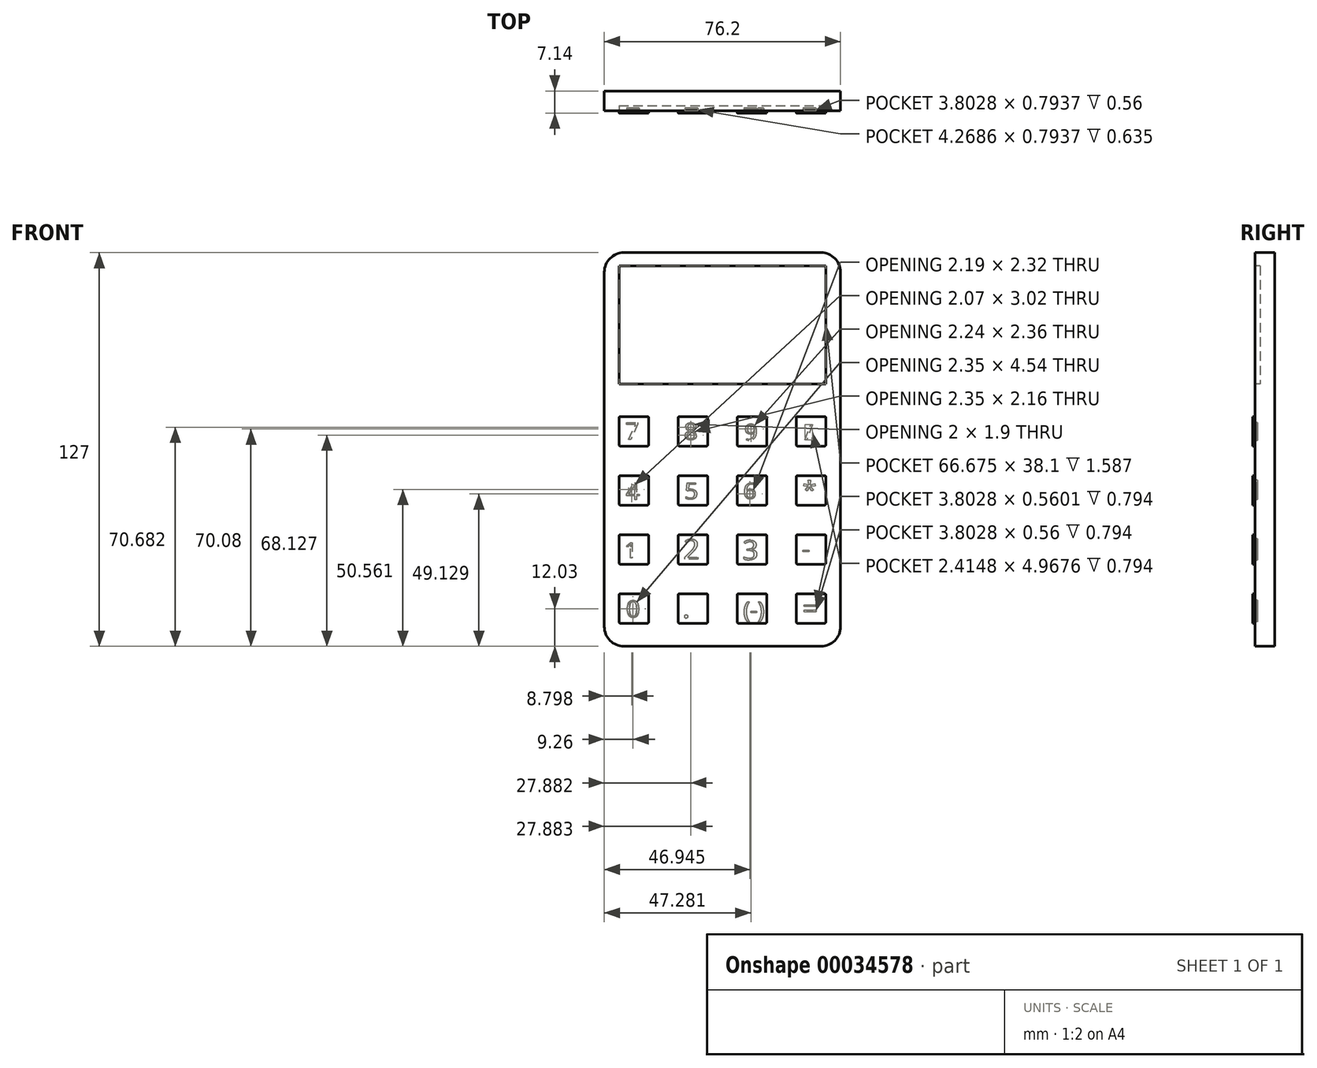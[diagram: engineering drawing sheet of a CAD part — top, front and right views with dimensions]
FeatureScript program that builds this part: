
annotation { "Feature Type Name" : "Feature", "Feature Type Description" : "" }
export const myFeature = defineFeature(function(context is Context, id is Id, definition is map)
    precondition{}
    {
        {
            var Q0;
            Q0=qCreatedBy(makeId("Front.planeOp"),FACE);
            var sketch = newSketch(context, id + "F0", { "sketchPlane" : qUnion([Q0])});
            skLineSegment(sketch, "E0.bottom", {"start": v(-54.14, 62.32) * mm, "end": v(22.06, 62.32) * mm});
            skLineSegment(sketch, "E0.top", {"start": v(-54.14, -64.68) * mm, "end": v(22.06, -64.68) * mm});
            skLineSegment(sketch, "E0.left", {"start": v(-54.14, 62.32) * mm, "end": v(-54.14, -64.68) * mm});
            skLineSegment(sketch, "E0.right", {"start": v(22.06, 62.32) * mm, "end": v(22.06, -64.68) * mm});
            skSolve(sketch);
        }
        {
            var Q0;
            Q0=makeQuery(id+"F0.imprint","IMPRINT",FACE,{"disambiguationData":[TD([[makeQuery(id+"F0.imprint","IMPRINT",EDGE,{"derivedFrom":sQuery(id+"F0.wireOp",EDGE,"E0.bottom")}),-1.0]])]});
            extrude(context, id + "F1", {"entities" : qUnion([Q0]), "depth" : 6.35 * mm});
        }
        {
            var Q0;
            Q0=makeQuery(id+"F1.opExtrude","CAP_FACE",FACE,{"disambiguationData":[OSD([sQuery(id+"F0.wireOp",EDGE,"E0.bottom"),sQuery(id+"F0.wireOp",EDGE,"E0.top"),sQuery(id+"F0.wireOp",EDGE,"E0.left"),sQuery(id+"F0.wireOp",EDGE,"E0.right")])],"isStart":false});
            var sketch = newSketch(context, id + "F2", { "sketchPlane" : qUnion([Q0])});
            skLineSegment(sketch, "E1.bottom", {"start": v(-49.38, 58.02) * mm, "end": v(17.3, 58.02) * mm});
            skLineSegment(sketch, "E1.top", {"start": v(-49.38, 19.92) * mm, "end": v(17.3, 19.92) * mm});
            skLineSegment(sketch, "E1.left", {"start": v(-49.38, 58.02) * mm, "end": v(-49.38, 19.92) * mm});
            skLineSegment(sketch, "E1.right", {"start": v(17.3, 58.02) * mm, "end": v(17.3, 19.92) * mm});
            skSolve(sketch);
        }
        {
            var Q0;
            Q0=makeQuery(id+"F2.imprint","IMPRINT",FACE,{"disambiguationData":[TD([[makeQuery(id+"F2.imprint","IMPRINT",EDGE,{"derivedFrom":sQuery(id+"F2.wireOp",EDGE,"E1.bottom")}),-1.0]])]});
            extrude(context, id + "F3", {"entities" : qUnion([Q0]), "operationType" : NewBodyOperationType.REMOVE, "oppositeDirection" : true, "depth" : 1.59 * mm});
        }
        {
            var Q0;
            Q0=makeQuery(id+"F1.opExtrude","SWEPT_EDGE",EDGE,{"disambiguationData":[OSD([sQuery(id+"F0.wireOp",EDGE,"E0.bottom"),sQuery(id+"F0.wireOp",EDGE,"E0.left")])]});
            var Q1;
            Q1=makeQuery(id+"F1.opExtrude","SWEPT_EDGE",EDGE,{"disambiguationData":[OSD([sQuery(id+"F0.wireOp",EDGE,"E0.bottom"),sQuery(id+"F0.wireOp",EDGE,"E0.right")])]});
            var Q2;
            Q2=makeQuery(id+"F1.opExtrude","SWEPT_EDGE",EDGE,{"disambiguationData":[OSD([sQuery(id+"F0.wireOp",EDGE,"E0.top"),sQuery(id+"F0.wireOp",EDGE,"E0.right")])]});
            var Q3;
            Q3=makeQuery(id+"F1.opExtrude","SWEPT_EDGE",EDGE,{"disambiguationData":[OSD([sQuery(id+"F0.wireOp",EDGE,"E0.top"),sQuery(id+"F0.wireOp",EDGE,"E0.left")])]});
            fillet(context, id + "F4", {"entities" : qUnion([Q0, Q1, Q2, Q3]), "radius" : 6.35 * mm, "tangentPropagation" : true, "allowEdgeOverflow" : false});
        }
        {
            var Q0;
            Q0=makeQuery(id+"F1.opExtrude","CAP_FACE",FACE,{"disambiguationData":[OSD([sQuery(id+"F0.wireOp",EDGE,"E0.bottom"),sQuery(id+"F0.wireOp",EDGE,"E0.top"),sQuery(id+"F0.wireOp",EDGE,"E0.left"),sQuery(id+"F0.wireOp",EDGE,"E0.right")])],"isStart":false});
            var sketch = newSketch(context, id + "F5", { "sketchPlane" : qUnion([Q0])});
            skLineSegment(sketch, "E2.bottom", {"start": v(-49.38, -47.74) * mm, "end": v(-39.86, -47.74) * mm});
            skLineSegment(sketch, "E2.top", {"start": v(-49.38, -57.27) * mm, "end": v(-39.86, -57.27) * mm});
            skLineSegment(sketch, "E2.left", {"start": v(-49.38, -47.74) * mm, "end": v(-49.38, -57.27) * mm});
            skLineSegment(sketch, "E2.right", {"start": v(-39.86, -47.74) * mm, "end": v(-39.86, -57.27) * mm});
            skLineSegment(sketch, "E3.0.1.0", {"start": v(-49.38, -28.7) * mm, "end": v(-49.38, -38.22) * mm});
            skLineSegment(sketch, "E3.0.1.1", {"start": v(-49.38, -38.22) * mm, "end": v(-39.86, -38.22) * mm});
            skLineSegment(sketch, "E3.0.1.2", {"start": v(-49.38, -28.7) * mm, "end": v(-39.86, -28.7) * mm});
            skLineSegment(sketch, "E3.0.1.3", {"start": v(-39.86, -28.7) * mm, "end": v(-39.86, -38.22) * mm});
            skLineSegment(sketch, "E3.0.2.0", {"start": v(-49.38, -9.64) * mm, "end": v(-49.38, -19.17) * mm});
            skLineSegment(sketch, "E3.0.2.1", {"start": v(-49.38, -19.17) * mm, "end": v(-39.86, -19.17) * mm});
            skLineSegment(sketch, "E3.0.2.2", {"start": v(-49.38, -9.64) * mm, "end": v(-39.86, -9.64) * mm});
            skLineSegment(sketch, "E3.0.2.3", {"start": v(-39.86, -9.64) * mm, "end": v(-39.86, -19.17) * mm});
            skLineSegment(sketch, "E3.0.3.0", {"start": v(-49.38, 9.4) * mm, "end": v(-49.38, -0.12) * mm});
            skLineSegment(sketch, "E3.0.3.1", {"start": v(-49.38, -0.12) * mm, "end": v(-39.86, -0.12) * mm});
            skLineSegment(sketch, "E3.0.3.2", {"start": v(-49.38, 9.4) * mm, "end": v(-39.86, 9.4) * mm});
            skLineSegment(sketch, "E3.0.3.3", {"start": v(-39.86, 9.4) * mm, "end": v(-39.86, -0.12) * mm});
            skLineSegment(sketch, "E3.1.0.0", {"start": v(-30.33, -47.74) * mm, "end": v(-30.33, -57.27) * mm});
            skLineSegment(sketch, "E3.1.0.1", {"start": v(-30.33, -57.27) * mm, "end": v(-20.8, -57.27) * mm});
            skLineSegment(sketch, "E3.1.0.2", {"start": v(-30.33, -47.74) * mm, "end": v(-20.8, -47.74) * mm});
            skLineSegment(sketch, "E3.1.0.3", {"start": v(-20.8, -47.74) * mm, "end": v(-20.8, -57.27) * mm});
            skLineSegment(sketch, "E3.1.1.0", {"start": v(-30.33, -28.7) * mm, "end": v(-30.33, -38.22) * mm});
            skLineSegment(sketch, "E3.1.1.1", {"start": v(-30.33, -38.22) * mm, "end": v(-20.8, -38.22) * mm});
            skLineSegment(sketch, "E3.1.1.2", {"start": v(-30.33, -28.7) * mm, "end": v(-20.8, -28.7) * mm});
            skLineSegment(sketch, "E3.1.1.3", {"start": v(-20.8, -28.7) * mm, "end": v(-20.8, -38.22) * mm});
            skLineSegment(sketch, "E3.1.2.0", {"start": v(-30.33, -9.64) * mm, "end": v(-30.33, -19.17) * mm});
            skLineSegment(sketch, "E3.1.2.1", {"start": v(-30.33, -19.17) * mm, "end": v(-20.8, -19.17) * mm});
            skLineSegment(sketch, "E3.1.2.2", {"start": v(-30.33, -9.64) * mm, "end": v(-20.8, -9.64) * mm});
            skLineSegment(sketch, "E3.1.2.3", {"start": v(-20.8, -9.64) * mm, "end": v(-20.8, -19.17) * mm});
            skLineSegment(sketch, "E3.1.3.0", {"start": v(-30.33, 9.4) * mm, "end": v(-30.33, -0.12) * mm});
            skLineSegment(sketch, "E3.1.3.1", {"start": v(-30.33, -0.12) * mm, "end": v(-20.8, -0.12) * mm});
            skLineSegment(sketch, "E3.1.3.2", {"start": v(-30.33, 9.4) * mm, "end": v(-20.8, 9.4) * mm});
            skLineSegment(sketch, "E3.1.3.3", {"start": v(-20.8, 9.4) * mm, "end": v(-20.8, -0.12) * mm});
            skLineSegment(sketch, "E3.2.0.0", {"start": v(-11.28, -47.74) * mm, "end": v(-11.28, -57.27) * mm});
            skLineSegment(sketch, "E3.2.0.1", {"start": v(-11.28, -57.27) * mm, "end": v(-1.76, -57.27) * mm});
            skLineSegment(sketch, "E3.2.0.2", {"start": v(-11.28, -47.74) * mm, "end": v(-1.76, -47.74) * mm});
            skLineSegment(sketch, "E3.2.0.3", {"start": v(-1.76, -47.74) * mm, "end": v(-1.76, -57.27) * mm});
            skLineSegment(sketch, "E3.2.1.0", {"start": v(-11.28, -28.7) * mm, "end": v(-11.28, -38.22) * mm});
            skLineSegment(sketch, "E3.2.1.1", {"start": v(-11.28, -38.22) * mm, "end": v(-1.76, -38.22) * mm});
            skLineSegment(sketch, "E3.2.1.2", {"start": v(-11.28, -28.7) * mm, "end": v(-1.76, -28.7) * mm});
            skLineSegment(sketch, "E3.2.1.3", {"start": v(-1.76, -28.7) * mm, "end": v(-1.76, -38.22) * mm});
            skLineSegment(sketch, "E3.2.2.0", {"start": v(-11.28, -9.64) * mm, "end": v(-11.28, -19.17) * mm});
            skLineSegment(sketch, "E3.2.2.1", {"start": v(-11.28, -19.17) * mm, "end": v(-1.76, -19.17) * mm});
            skLineSegment(sketch, "E3.2.2.2", {"start": v(-11.28, -9.64) * mm, "end": v(-1.76, -9.64) * mm});
            skLineSegment(sketch, "E3.2.2.3", {"start": v(-1.76, -9.64) * mm, "end": v(-1.76, -19.17) * mm});
            skLineSegment(sketch, "E3.2.3.0", {"start": v(-11.28, 9.4) * mm, "end": v(-11.28, -0.12) * mm});
            skLineSegment(sketch, "E3.2.3.1", {"start": v(-11.28, -0.12) * mm, "end": v(-1.76, -0.12) * mm});
            skLineSegment(sketch, "E3.2.3.2", {"start": v(-11.28, 9.4) * mm, "end": v(-1.76, 9.4) * mm});
            skLineSegment(sketch, "E3.2.3.3", {"start": v(-1.76, 9.4) * mm, "end": v(-1.76, -0.12) * mm});
            skLineSegment(sketch, "E3.3.0.0", {"start": v(7.77, -47.74) * mm, "end": v(7.77, -57.27) * mm});
            skLineSegment(sketch, "E3.3.0.1", {"start": v(7.77, -57.27) * mm, "end": v(17.3, -57.27) * mm});
            skLineSegment(sketch, "E3.3.0.2", {"start": v(7.77, -47.74) * mm, "end": v(17.3, -47.74) * mm});
            skLineSegment(sketch, "E3.3.0.3", {"start": v(17.3, -47.74) * mm, "end": v(17.3, -57.27) * mm});
            skLineSegment(sketch, "E3.3.1.0", {"start": v(7.77, -28.7) * mm, "end": v(7.77, -38.22) * mm});
            skLineSegment(sketch, "E3.3.1.1", {"start": v(7.77, -38.22) * mm, "end": v(17.3, -38.22) * mm});
            skLineSegment(sketch, "E3.3.1.2", {"start": v(7.77, -28.7) * mm, "end": v(17.3, -28.7) * mm});
            skLineSegment(sketch, "E3.3.1.3", {"start": v(17.3, -28.7) * mm, "end": v(17.3, -38.22) * mm});
            skLineSegment(sketch, "E3.3.2.0", {"start": v(7.77, -9.64) * mm, "end": v(7.77, -19.17) * mm});
            skLineSegment(sketch, "E3.3.2.1", {"start": v(7.77, -19.17) * mm, "end": v(17.3, -19.17) * mm});
            skLineSegment(sketch, "E3.3.2.2", {"start": v(7.77, -9.64) * mm, "end": v(17.3, -9.64) * mm});
            skLineSegment(sketch, "E3.3.2.3", {"start": v(17.3, -9.64) * mm, "end": v(17.3, -19.17) * mm});
            skLineSegment(sketch, "E3.3.3.0", {"start": v(7.77, 9.4) * mm, "end": v(7.77, -0.12) * mm});
            skLineSegment(sketch, "E3.3.3.1", {"start": v(7.77, -0.12) * mm, "end": v(17.3, -0.12) * mm});
            skLineSegment(sketch, "E3.3.3.2", {"start": v(7.77, 9.4) * mm, "end": v(17.3, 9.4) * mm});
            skLineSegment(sketch, "E3.3.3.3", {"start": v(17.3, 9.4) * mm, "end": v(17.3, -0.12) * mm});
            skLineSegment(sketch, "E3.direction1", {"start": v(-49.38, -57.27) * mm, "end": v(-30.33, -57.27) * mm, "construction": true});
            skLineSegment(sketch, "E3.direction2", {"start": v(-49.38, -57.27) * mm, "end": v(-49.38, -38.22) * mm, "construction": true});
            skSolve(sketch);
        }
        {
            var Q0;
            Q0 = qSketchRegion(id + "F5", true);
            extrude(context, id + "F6", {"entities" : qUnion([Q0]), "operationType" : NewBodyOperationType.ADD, "depth" : 0.8 * mm});
        }
        {
            var Q0;
            Q0=makeQuery(id+"F6.opExtrude","SWEPT_EDGE",EDGE,{"disambiguationData":[OSD([sQuery(id+"F5.wireOp",EDGE,"E3.0.3.0"),sQuery(id+"F5.wireOp",EDGE,"E3.0.3.2")])]});
            var Q1;
            Q1=makeQuery(id+"F6.opExtrude","SWEPT_EDGE",EDGE,{"disambiguationData":[OSD([sQuery(id+"F5.wireOp",EDGE,"E3.0.2.0"),sQuery(id+"F5.wireOp",EDGE,"E3.0.2.2")])]});
            var Q2;
            Q2=makeQuery(id+"F6.opExtrude","SWEPT_EDGE",EDGE,{"disambiguationData":[OSD([sQuery(id+"F5.wireOp",EDGE,"E3.0.1.0"),sQuery(id+"F5.wireOp",EDGE,"E3.0.1.2")])]});
            var Q3;
            Q3=makeQuery(id+"F6.opExtrude","SWEPT_EDGE",EDGE,{"disambiguationData":[OSD([sQuery(id+"F5.wireOp",EDGE,"E2.bottom"),sQuery(id+"F5.wireOp",EDGE,"E2.left")])]});
            var Q4;
            Q4=makeQuery(id+"F6.opExtrude","SWEPT_EDGE",EDGE,{"disambiguationData":[OSD([sQuery(id+"F5.wireOp",EDGE,"E2.top"),sQuery(id+"F5.wireOp",EDGE,"E2.left")])]});
            var Q5;
            Q5=makeQuery(id+"F6.opExtrude","SWEPT_EDGE",EDGE,{"disambiguationData":[OSD([sQuery(id+"F5.wireOp",EDGE,"E3.1.0.0"),sQuery(id+"F5.wireOp",EDGE,"E3.1.0.1")])]});
            var Q6;
            Q6=makeQuery(id+"F6.opExtrude","SWEPT_EDGE",EDGE,{"disambiguationData":[OSD([sQuery(id+"F5.wireOp",EDGE,"E3.1.1.0"),sQuery(id+"F5.wireOp",EDGE,"E3.1.1.1")])]});
            var Q7;
            Q7=makeQuery(id+"F6.opExtrude","SWEPT_EDGE",EDGE,{"disambiguationData":[OSD([sQuery(id+"F5.wireOp",EDGE,"E3.0.1.0"),sQuery(id+"F5.wireOp",EDGE,"E3.0.1.1")])]});
            var Q8;
            Q8=makeQuery(id+"F6.opExtrude","SWEPT_EDGE",EDGE,{"disambiguationData":[OSD([sQuery(id+"F5.wireOp",EDGE,"E3.2.1.0"),sQuery(id+"F5.wireOp",EDGE,"E3.2.1.1")])]});
            var Q9;
            Q9=makeQuery(id+"F6.opExtrude","SWEPT_EDGE",EDGE,{"disambiguationData":[OSD([sQuery(id+"F5.wireOp",EDGE,"E3.2.0.0"),sQuery(id+"F5.wireOp",EDGE,"E3.2.0.1")])]});
            var Q10;
            Q10=makeQuery(id+"F6.opExtrude","SWEPT_EDGE",EDGE,{"disambiguationData":[OSD([sQuery(id+"F5.wireOp",EDGE,"E3.2.2.0"),sQuery(id+"F5.wireOp",EDGE,"E3.2.2.1")])]});
            var Q11;
            Q11=makeQuery(id+"F6.opExtrude","SWEPT_EDGE",EDGE,{"disambiguationData":[OSD([sQuery(id+"F5.wireOp",EDGE,"E3.1.2.0"),sQuery(id+"F5.wireOp",EDGE,"E3.1.2.1")])]});
            var Q12;
            Q12=makeQuery(id+"F6.opExtrude","SWEPT_EDGE",EDGE,{"disambiguationData":[OSD([sQuery(id+"F5.wireOp",EDGE,"E3.0.2.0"),sQuery(id+"F5.wireOp",EDGE,"E3.0.2.1")])]});
            var Q13;
            Q13=makeQuery(id+"F6.opExtrude","SWEPT_EDGE",EDGE,{"disambiguationData":[OSD([sQuery(id+"F5.wireOp",EDGE,"E3.0.3.0"),sQuery(id+"F5.wireOp",EDGE,"E3.0.3.1")])]});
            var Q14;
            Q14=makeQuery(id+"F6.opExtrude","SWEPT_EDGE",EDGE,{"disambiguationData":[OSD([sQuery(id+"F5.wireOp",EDGE,"E3.0.3.1"),sQuery(id+"F5.wireOp",EDGE,"E3.0.3.3")])]});
            var Q15;
            Q15=makeQuery(id+"F6.opExtrude","SWEPT_EDGE",EDGE,{"disambiguationData":[OSD([sQuery(id+"F5.wireOp",EDGE,"E3.0.2.1"),sQuery(id+"F5.wireOp",EDGE,"E3.0.2.3")])]});
            var Q16;
            Q16=makeQuery(id+"F6.opExtrude","SWEPT_EDGE",EDGE,{"disambiguationData":[OSD([sQuery(id+"F5.wireOp",EDGE,"E3.0.1.1"),sQuery(id+"F5.wireOp",EDGE,"E3.0.1.3")])]});
            var Q17;
            Q17=makeQuery(id+"F6.opExtrude","SWEPT_EDGE",EDGE,{"disambiguationData":[OSD([sQuery(id+"F5.wireOp",EDGE,"E2.top"),sQuery(id+"F5.wireOp",EDGE,"E2.right")])]});
            var Q18;
            Q18=makeQuery(id+"F6.opExtrude","SWEPT_EDGE",EDGE,{"disambiguationData":[OSD([sQuery(id+"F5.wireOp",EDGE,"E2.bottom"),sQuery(id+"F5.wireOp",EDGE,"E2.right")])]});
            var Q19;
            Q19=makeQuery(id+"F6.opExtrude","SWEPT_EDGE",EDGE,{"disambiguationData":[OSD([sQuery(id+"F5.wireOp",EDGE,"E3.0.1.2"),sQuery(id+"F5.wireOp",EDGE,"E3.0.1.3")])]});
            var Q20;
            Q20=makeQuery(id+"F6.opExtrude","SWEPT_EDGE",EDGE,{"disambiguationData":[OSD([sQuery(id+"F5.wireOp",EDGE,"E3.0.2.2"),sQuery(id+"F5.wireOp",EDGE,"E3.0.2.3")])]});
            var Q21;
            Q21=makeQuery(id+"F6.opExtrude","SWEPT_EDGE",EDGE,{"disambiguationData":[OSD([sQuery(id+"F5.wireOp",EDGE,"E3.0.3.2"),sQuery(id+"F5.wireOp",EDGE,"E3.0.3.3")])]});
            var Q22;
            Q22=makeQuery(id+"F6.opExtrude","SWEPT_EDGE",EDGE,{"disambiguationData":[OSD([sQuery(id+"F5.wireOp",EDGE,"E3.1.0.2"),sQuery(id+"F5.wireOp",EDGE,"E3.1.0.3")])]});
            var Q23;
            Q23=makeQuery(id+"F6.opExtrude","SWEPT_EDGE",EDGE,{"disambiguationData":[OSD([sQuery(id+"F5.wireOp",EDGE,"E3.1.1.2"),sQuery(id+"F5.wireOp",EDGE,"E3.1.1.3")])]});
            var Q24;
            Q24=makeQuery(id+"F6.opExtrude","SWEPT_EDGE",EDGE,{"disambiguationData":[OSD([sQuery(id+"F5.wireOp",EDGE,"E3.1.2.2"),sQuery(id+"F5.wireOp",EDGE,"E3.1.2.3")])]});
            var Q25;
            Q25=makeQuery(id+"F6.opExtrude","SWEPT_EDGE",EDGE,{"disambiguationData":[OSD([sQuery(id+"F5.wireOp",EDGE,"E3.1.3.2"),sQuery(id+"F5.wireOp",EDGE,"E3.1.3.3")])]});
            var Q26;
            Q26=makeQuery(id+"F6.opExtrude","SWEPT_EDGE",EDGE,{"disambiguationData":[OSD([sQuery(id+"F5.wireOp",EDGE,"E3.2.3.2"),sQuery(id+"F5.wireOp",EDGE,"E3.2.3.3")])]});
            var Q27;
            Q27=makeQuery(id+"F6.opExtrude","SWEPT_EDGE",EDGE,{"disambiguationData":[OSD([sQuery(id+"F5.wireOp",EDGE,"E3.3.3.2"),sQuery(id+"F5.wireOp",EDGE,"E3.3.3.3")])]});
            var Q28;
            Q28=makeQuery(id+"F6.opExtrude","SWEPT_EDGE",EDGE,{"disambiguationData":[OSD([sQuery(id+"F5.wireOp",EDGE,"E3.2.1.1"),sQuery(id+"F5.wireOp",EDGE,"E3.2.1.3")])]});
            var Q29;
            Q29=makeQuery(id+"F6.opExtrude","SWEPT_EDGE",EDGE,{"disambiguationData":[OSD([sQuery(id+"F5.wireOp",EDGE,"E3.2.2.1"),sQuery(id+"F5.wireOp",EDGE,"E3.2.2.3")])]});
            var Q30;
            Q30=makeQuery(id+"F6.opExtrude","SWEPT_EDGE",EDGE,{"disambiguationData":[OSD([sQuery(id+"F5.wireOp",EDGE,"E3.3.2.1"),sQuery(id+"F5.wireOp",EDGE,"E3.3.2.3")])]});
            var Q31;
            Q31=makeQuery(id+"F6.opExtrude","SWEPT_EDGE",EDGE,{"disambiguationData":[OSD([sQuery(id+"F5.wireOp",EDGE,"E3.3.1.1"),sQuery(id+"F5.wireOp",EDGE,"E3.3.1.3")])]});
            var Q32;
            Q32=makeQuery(id+"F6.opExtrude","SWEPT_EDGE",EDGE,{"disambiguationData":[OSD([sQuery(id+"F5.wireOp",EDGE,"E3.1.3.1"),sQuery(id+"F5.wireOp",EDGE,"E3.1.3.3")])]});
            var Q33;
            Q33=makeQuery(id+"F6.opExtrude","SWEPT_EDGE",EDGE,{"disambiguationData":[OSD([sQuery(id+"F5.wireOp",EDGE,"E3.1.2.1"),sQuery(id+"F5.wireOp",EDGE,"E3.1.2.3")])]});
            var Q34;
            Q34=makeQuery(id+"F6.opExtrude","SWEPT_EDGE",EDGE,{"disambiguationData":[OSD([sQuery(id+"F5.wireOp",EDGE,"E3.1.1.1"),sQuery(id+"F5.wireOp",EDGE,"E3.1.1.3")])]});
            var Q35;
            Q35=makeQuery(id+"F6.opExtrude","SWEPT_EDGE",EDGE,{"disambiguationData":[OSD([sQuery(id+"F5.wireOp",EDGE,"E3.1.0.1"),sQuery(id+"F5.wireOp",EDGE,"E3.1.0.3")])]});
            var Q36;
            Q36=makeQuery(id+"F6.opExtrude","SWEPT_EDGE",EDGE,{"disambiguationData":[OSD([sQuery(id+"F5.wireOp",EDGE,"E3.1.0.0"),sQuery(id+"F5.wireOp",EDGE,"E3.1.0.2")])]});
            var Q37;
            Q37=makeQuery(id+"F6.opExtrude","SWEPT_EDGE",EDGE,{"disambiguationData":[OSD([sQuery(id+"F5.wireOp",EDGE,"E3.1.1.0"),sQuery(id+"F5.wireOp",EDGE,"E3.1.1.2")])]});
            var Q38;
            Q38=makeQuery(id+"F6.opExtrude","SWEPT_EDGE",EDGE,{"disambiguationData":[OSD([sQuery(id+"F5.wireOp",EDGE,"E3.1.2.0"),sQuery(id+"F5.wireOp",EDGE,"E3.1.2.2")])]});
            var Q39;
            Q39=makeQuery(id+"F6.opExtrude","SWEPT_EDGE",EDGE,{"disambiguationData":[OSD([sQuery(id+"F5.wireOp",EDGE,"E3.1.3.0"),sQuery(id+"F5.wireOp",EDGE,"E3.1.3.2")])]});
            var Q40;
            Q40=makeQuery(id+"F6.opExtrude","SWEPT_EDGE",EDGE,{"disambiguationData":[OSD([sQuery(id+"F5.wireOp",EDGE,"E3.2.0.0"),sQuery(id+"F5.wireOp",EDGE,"E3.2.0.2")])]});
            var Q41;
            Q41=makeQuery(id+"F6.opExtrude","SWEPT_EDGE",EDGE,{"disambiguationData":[OSD([sQuery(id+"F5.wireOp",EDGE,"E3.2.0.1"),sQuery(id+"F5.wireOp",EDGE,"E3.2.0.3")])]});
            var Q42;
            Q42=makeQuery(id+"F6.opExtrude","SWEPT_EDGE",EDGE,{"disambiguationData":[OSD([sQuery(id+"F5.wireOp",EDGE,"E3.2.0.2"),sQuery(id+"F5.wireOp",EDGE,"E3.2.0.3")])]});
            var Q43;
            Q43=makeQuery(id+"F6.opExtrude","SWEPT_EDGE",EDGE,{"disambiguationData":[OSD([sQuery(id+"F5.wireOp",EDGE,"E3.2.1.2"),sQuery(id+"F5.wireOp",EDGE,"E3.2.1.3")])]});
            var Q44;
            Q44=makeQuery(id+"F6.opExtrude","SWEPT_EDGE",EDGE,{"disambiguationData":[OSD([sQuery(id+"F5.wireOp",EDGE,"E3.2.1.0"),sQuery(id+"F5.wireOp",EDGE,"E3.2.1.2")])]});
            var Q45;
            Q45=makeQuery(id+"F6.opExtrude","SWEPT_EDGE",EDGE,{"disambiguationData":[OSD([sQuery(id+"F5.wireOp",EDGE,"E3.2.2.0"),sQuery(id+"F5.wireOp",EDGE,"E3.2.2.2")])]});
            var Q46;
            Q46=makeQuery(id+"F6.opExtrude","SWEPT_EDGE",EDGE,{"disambiguationData":[OSD([sQuery(id+"F5.wireOp",EDGE,"E3.2.2.2"),sQuery(id+"F5.wireOp",EDGE,"E3.2.2.3")])]});
            var Q47;
            Q47=makeQuery(id+"F6.opExtrude","SWEPT_EDGE",EDGE,{"disambiguationData":[OSD([sQuery(id+"F5.wireOp",EDGE,"E3.2.3.0"),sQuery(id+"F5.wireOp",EDGE,"E3.2.3.2")])]});
            var Q48;
            Q48=makeQuery(id+"F6.opExtrude","SWEPT_EDGE",EDGE,{"disambiguationData":[OSD([sQuery(id+"F5.wireOp",EDGE,"E3.2.3.0"),sQuery(id+"F5.wireOp",EDGE,"E3.2.3.1")])]});
            var Q49;
            Q49=makeQuery(id+"F6.opExtrude","SWEPT_EDGE",EDGE,{"disambiguationData":[OSD([sQuery(id+"F5.wireOp",EDGE,"E3.2.3.1"),sQuery(id+"F5.wireOp",EDGE,"E3.2.3.3")])]});
            var Q50;
            Q50=makeQuery(id+"F6.opExtrude","SWEPT_EDGE",EDGE,{"disambiguationData":[OSD([sQuery(id+"F5.wireOp",EDGE,"E3.3.3.0"),sQuery(id+"F5.wireOp",EDGE,"E3.3.3.2")])]});
            var Q51;
            Q51=makeQuery(id+"F6.opExtrude","SWEPT_EDGE",EDGE,{"disambiguationData":[OSD([sQuery(id+"F5.wireOp",EDGE,"E3.3.3.0"),sQuery(id+"F5.wireOp",EDGE,"E3.3.3.1")])]});
            var Q52;
            Q52=makeQuery(id+"F6.opExtrude","SWEPT_EDGE",EDGE,{"disambiguationData":[OSD([sQuery(id+"F5.wireOp",EDGE,"E3.3.3.1"),sQuery(id+"F5.wireOp",EDGE,"E3.3.3.3")])]});
            var Q53;
            Q53=makeQuery(id+"F6.opExtrude","SWEPT_EDGE",EDGE,{"disambiguationData":[OSD([sQuery(id+"F5.wireOp",EDGE,"E3.3.2.2"),sQuery(id+"F5.wireOp",EDGE,"E3.3.2.3")])]});
            var Q54;
            Q54=makeQuery(id+"F6.opExtrude","SWEPT_EDGE",EDGE,{"disambiguationData":[OSD([sQuery(id+"F5.wireOp",EDGE,"E3.3.2.0"),sQuery(id+"F5.wireOp",EDGE,"E3.3.2.2")])]});
            var Q55;
            Q55=makeQuery(id+"F6.opExtrude","SWEPT_EDGE",EDGE,{"disambiguationData":[OSD([sQuery(id+"F5.wireOp",EDGE,"E3.3.2.0"),sQuery(id+"F5.wireOp",EDGE,"E3.3.2.1")])]});
            var Q56;
            Q56=makeQuery(id+"F6.opExtrude","SWEPT_EDGE",EDGE,{"disambiguationData":[OSD([sQuery(id+"F5.wireOp",EDGE,"E3.1.3.0"),sQuery(id+"F5.wireOp",EDGE,"E3.1.3.1")])]});
            var Q57;
            Q57=makeQuery(id+"F6.opExtrude","SWEPT_EDGE",EDGE,{"disambiguationData":[OSD([sQuery(id+"F5.wireOp",EDGE,"E3.3.1.0"),sQuery(id+"F5.wireOp",EDGE,"E3.3.1.1")])]});
            var Q58;
            Q58=makeQuery(id+"F6.opExtrude","SWEPT_EDGE",EDGE,{"disambiguationData":[OSD([sQuery(id+"F5.wireOp",EDGE,"E3.3.0.0"),sQuery(id+"F5.wireOp",EDGE,"E3.3.0.1")])]});
            var Q59;
            Q59=makeQuery(id+"F6.opExtrude","SWEPT_EDGE",EDGE,{"disambiguationData":[OSD([sQuery(id+"F5.wireOp",EDGE,"E3.3.0.0"),sQuery(id+"F5.wireOp",EDGE,"E3.3.0.2")])]});
            var Q60;
            Q60=makeQuery(id+"F6.opExtrude","SWEPT_EDGE",EDGE,{"disambiguationData":[OSD([sQuery(id+"F5.wireOp",EDGE,"E3.3.1.0"),sQuery(id+"F5.wireOp",EDGE,"E3.3.1.2")])]});
            var Q61;
            Q61=makeQuery(id+"F6.opExtrude","SWEPT_EDGE",EDGE,{"disambiguationData":[OSD([sQuery(id+"F5.wireOp",EDGE,"E3.3.0.1"),sQuery(id+"F5.wireOp",EDGE,"E3.3.0.3")])]});
            var Q62;
            Q62=makeQuery(id+"F6.opExtrude","SWEPT_EDGE",EDGE,{"disambiguationData":[OSD([sQuery(id+"F5.wireOp",EDGE,"E3.3.0.2"),sQuery(id+"F5.wireOp",EDGE,"E3.3.0.3")])]});
            var Q63;
            Q63=makeQuery(id+"F6.opExtrude","SWEPT_EDGE",EDGE,{"disambiguationData":[OSD([sQuery(id+"F5.wireOp",EDGE,"E3.3.1.2"),sQuery(id+"F5.wireOp",EDGE,"E3.3.1.3")])]});
            fillet(context, id + "F7", {"entities" : qUnion([Q0, Q1, Q2, Q3, Q4, Q5, Q6, Q7, Q8, Q9, Q10, Q11, Q12, Q13, Q14, Q15, Q16, Q17, Q18, Q19, Q20, Q21, Q22, Q23, Q24, Q25, Q26, Q27, Q28, Q29, Q30, Q31, Q32, Q33, Q34, Q35, Q36, Q37, Q38, Q39, Q40, Q41, Q42, Q43, Q44, Q45, Q46, Q47, Q48, Q49, Q50, Q51, Q52, Q53, Q54, Q55, Q56, Q57, Q58, Q59, Q60, Q61, Q62, Q63]), "radius" : 0.4 * mm, "tangentPropagation" : true, "allowEdgeOverflow" : false});
        }
        {
            var Q0;
            Q0=makeQuery(id+"F1.opExtrude","CAP_FACE",FACE,{"disambiguationData":[OSD([sQuery(id+"F0.wireOp",EDGE,"E0.bottom"),sQuery(id+"F0.wireOp",EDGE,"E0.top"),sQuery(id+"F0.wireOp",EDGE,"E0.left"),sQuery(id+"F0.wireOp",EDGE,"E0.right")])],"isStart":false});
            var sketch = newSketch(context, id + "F8", { "sketchPlane" : qUnion([Q0])});
            skText(sketch, "E4", { "text": "7\n", "fontName": "OpenSans-Regular.ttf"});
            skText(sketch, "E5", { "text": "8", "fontName": "OpenSans-Regular.ttf"});
            skText(sketch, "E6", { "text": "9", "fontName": "OpenSans-Regular.ttf"});
            skText(sketch, "E7", { "text": "/", "fontName": "OpenSans-Regular.ttf"});
            skText(sketch, "E8", { "text": "4", "fontName": "OpenSans-Regular.ttf"});
            skText(sketch, "E9", { "text": "5", "fontName": "OpenSans-Regular.ttf"});
            skText(sketch, "E10", { "text": "6", "fontName": "OpenSans-Regular.ttf"});
            skText(sketch, "E11", { "text": "*", "fontName": "OpenSans-Regular.ttf"});
            skText(sketch, "E12", { "text": "1\n", "fontName": "OpenSans-Regular.ttf"});
            skText(sketch, "E13", { "text": "2", "fontName": "OpenSans-Regular.ttf"});
            skText(sketch, "E14", { "text": "3", "fontName": "OpenSans-Regular.ttf"});
            skText(sketch, "E15", { "text": "-", "fontName": "OpenSans-Regular.ttf"});
            skText(sketch, "E16", { "text": "0", "fontName": "OpenSans-Regular.ttf"});
            skText(sketch, "E17", { "text": ".", "fontName": "OpenSans-Regular.ttf"});
            skText(sketch, "E18", { "text": "(-)", "fontName": "OpenSans-Regular.ttf"});
            skText(sketch, "E19", { "text": "=", "fontName": "OpenSans-Regular.ttf"});
            const initialGuessF8  = {"E4": [-0.04733, 0.00204, 1, 0, 0.00548], "E5": [-0.02843, 0.00194, 1, 0, 0.00548], "E6": [-0.00895, 0.00176, 1, 0, 0.0053], "E7": [0.01052, 0.00185, 1, 0, 0.00501], "E8": [-0.04716, -0.01745, 1, 0, 0.00551], "E9": [-0.02823, -0.01724, 1, 0, 0.0054], "E10": [-0.0093, -0.01714, 1, 0, 0.0052], "E11": [0.00983, -0.01714, 1, 0, 0.00572], "E12": [-0.0476, -0.03615, 1, 0, 0.005], "E13": [-0.02864, -0.03661, 1, 0, 0.00655], "E14": [-0.00951, -0.03675, 1, 0, 0.00629], "E15": [0.00962, -0.03602, 1, 0, 0.00557], "E16": [-0.04706, -0.05538, 1, 0, 0.0055], "E17": [-0.02884, -0.0555, 1, 0, 0.00603], "E18": [-0.00932, -0.05564, 1, 0, 0.00537], "E19": [0.0098, -0.05538, 1, 0, 0.00603]};
            skSetInitialGuess(sketch, initialGuessF8);
            skSolve(sketch);
        }
        {
            var Q0;
            Q0 = qSketchRegion(id + "F8", true);
            extrude(context, id + "F9", {"entities" : qUnion([Q0]), "operationType" : NewBodyOperationType.REMOVE, "oppositeDirection" : true, "depth" : 0.8 * mm});
        }
    });
